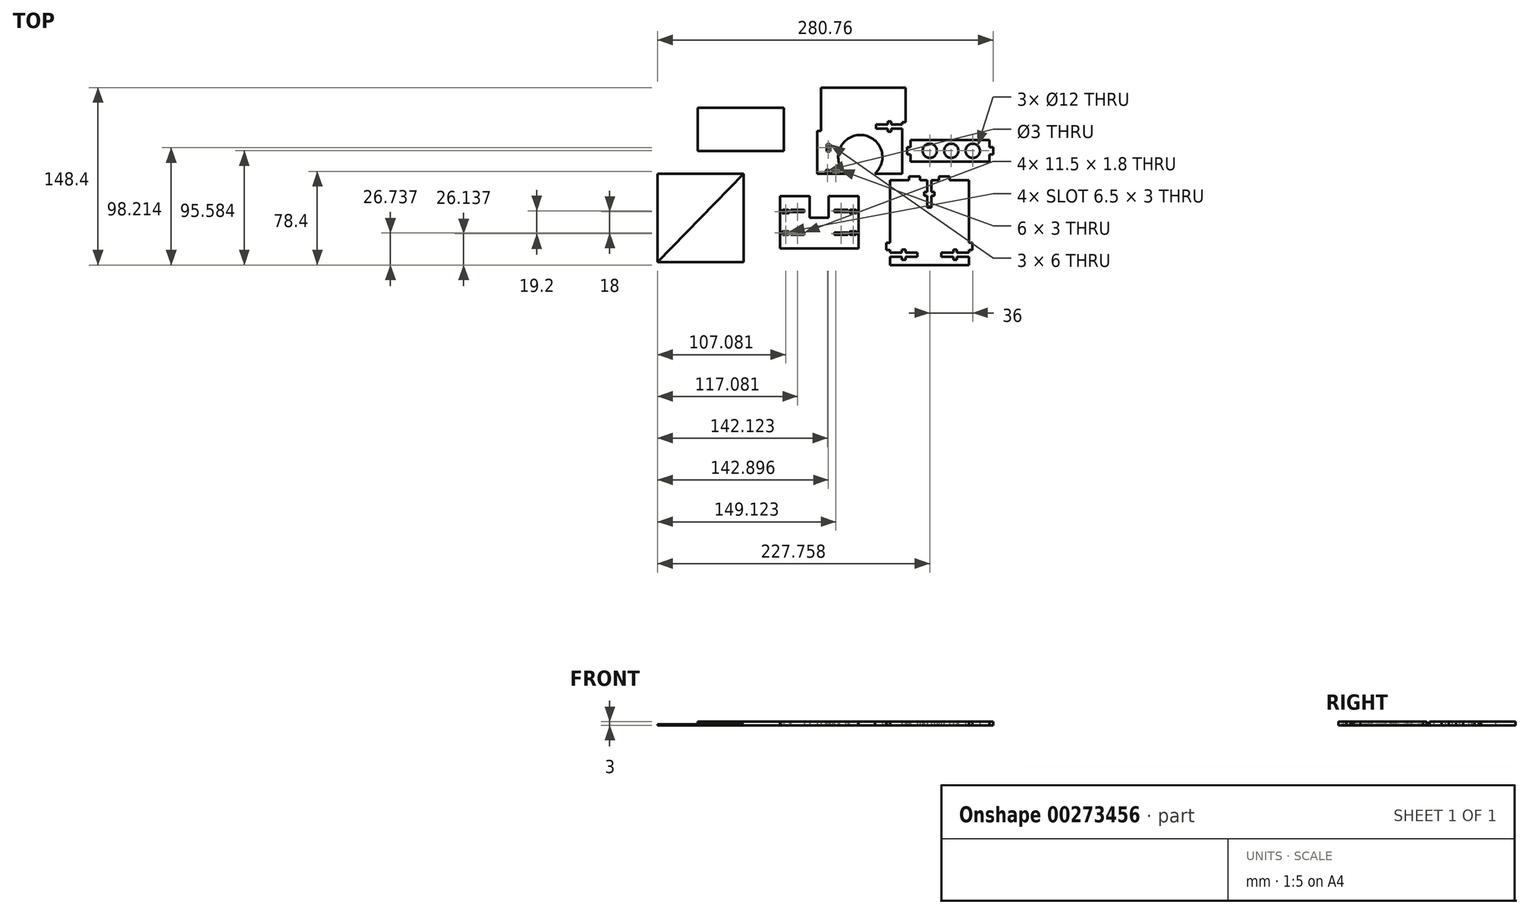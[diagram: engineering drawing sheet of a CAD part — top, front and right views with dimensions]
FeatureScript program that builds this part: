
annotation { "Feature Type Name" : "Feature", "Feature Type Description" : "" }
export const myFeature = defineFeature(function(context is Context, id is Id, definition is map)
    precondition{}
    {
        {
            var Q0;
            Q0=qCreatedBy(makeId("Top.planeOp"),FACE);
            var sketch = newSketch(context, id + "F0", { "sketchPlane" : qUnion([Q0])});
            skLineSegment(sketch, "E0", {"start": v(0, 0) * mm, "end": v(31.91, 0) * mm});
            skLineSegment(sketch, "E1", {"start": v(31.91, 0) * mm, "end": v(31.91, 36) * mm});
            skLineSegment(sketch, "E2", {"start": v(31.91, 36) * mm, "end": v(34.91, 36) * mm});
            skLineSegment(sketch, "E3", {"start": v(34.91, 36) * mm, "end": v(34.91, 72) * mm});
            skLineSegment(sketch, "E4", {"start": v(34.91, 72) * mm, "end": v(-36.09, 72) * mm});
            skLineSegment(sketch, "E5", {"start": v(-36.09, 72) * mm, "end": v(-36.09, 36) * mm});
            skLineSegment(sketch, "E6", {"start": v(-36.09, 36) * mm, "end": v(-39.09, 36) * mm});
            skLineSegment(sketch, "E7", {"start": v(-39.09, 36) * mm, "end": v(-39.09, 0) * mm});
            skLineSegment(sketch, "E8", {"start": v(-39.09, 0) * mm, "end": v(0, 0) * mm});
            skSolve(sketch);
        }
        {
            var Q0;
            Q0=makeQuery(id+"F0.imprint","IMPRINT",FACE,{"disambiguationData":[TD([[makeQuery(id+"F0.imprint","IMPRINT",EDGE,{"derivedFrom":sQuery(id+"F0.wireOp",EDGE,"E0")}),1.0]])]});
            extrude(context, id + "F1", {"entities" : qUnion([Q0]), "depth" : 3 * mm});
        }
        {
            var Q0;
            Q0=makeQuery(id+"F0.imprint","IMPRINT",FACE,{"disambiguationData":[TD([[makeQuery(id+"F0.imprint","IMPRINT",EDGE,{"derivedFrom":sQuery(id+"F0.wireOp",EDGE,"E0")}),1.0]])]});
            var sketch = newSketch(context, id + "F2", { "sketchPlane" : qUnion([Q0])});
            skCircle(sketch, "E9", {"center": v(-3.09, 14) * mm, "radius": 18.5 * mm});
            skCircle(sketch, "E10", {"center": v(-30.59, 2) * mm, "radius": 1.5 * mm});
            skLineSegment(sketch, "E11.bottom", {"start": v(-26.59, 3.5) * mm, "end": v(-20.59, 3.5) * mm});
            skLineSegment(sketch, "E11.top", {"start": v(-26.59, 0.5) * mm, "end": v(-20.59, 0.5) * mm});
            skLineSegment(sketch, "E11.left", {"start": v(-26.59, 3.5) * mm, "end": v(-26.59, 0.5) * mm});
            skLineSegment(sketch, "E11.right", {"start": v(-20.59, 3.5) * mm, "end": v(-20.59, 0.5) * mm});
            skLineSegment(sketch, "E12.bottom", {"start": v(-31.31, 24.81) * mm, "end": v(-28.31, 24.81) * mm});
            skLineSegment(sketch, "E12.top", {"start": v(-31.31, 18.81) * mm, "end": v(-28.31, 18.81) * mm});
            skLineSegment(sketch, "E12.left", {"start": v(-31.31, 24.81) * mm, "end": v(-31.31, 18.81) * mm});
            skLineSegment(sketch, "E12.right", {"start": v(-28.31, 24.81) * mm, "end": v(-28.31, 18.81) * mm});
            skSolve(sketch);
        }
        {
            var Q0;
            Q0 = qSketchRegion(id + "F2", true);
            extrude(context, id + "F3", {"entities" : qUnion([Q0]), "operationType" : NewBodyOperationType.REMOVE, "endBound" : BoundingType.UP_TO_NEXT, "depth" : 25 * mm});
        }
        {
            var Q0;
            Q0=makeQuery(id+"F1.opExtrude","CAP_FACE",FACE,{"disambiguationData":[OSD([sQuery(id+"F0.wireOp",EDGE,"E0"),sQuery(id+"F0.wireOp",EDGE,"E1"),sQuery(id+"F0.wireOp",EDGE,"E2"),sQuery(id+"F0.wireOp",EDGE,"E3"),sQuery(id+"F0.wireOp",EDGE,"E4"),sQuery(id+"F0.wireOp",EDGE,"E5"),sQuery(id+"F0.wireOp",EDGE,"E6"),sQuery(id+"F0.wireOp",EDGE,"E7"),sQuery(id+"F0.wireOp",EDGE,"E8")])],"isStart":false});
            var sketch = newSketch(context, id + "F4", { "sketchPlane" : qUnion([Q0])});
            skLineSegment(sketch, "E13", {"start": v(22.91, 41.25) * mm, "end": v(22.91, 43.75) * mm});
            skLineSegment(sketch, "E14", {"start": v(22.91, 43.75) * mm, "end": v(19.91, 43.75) * mm});
            skLineSegment(sketch, "E15", {"start": v(19.91, 43.75) * mm, "end": v(19.91, 41.25) * mm});
            skLineSegment(sketch, "E16", {"start": v(19.91, 41.25) * mm, "end": v(9.91, 41.25) * mm});
            skLineSegment(sketch, "E17", {"start": v(9.91, 41.25) * mm, "end": v(9.91, 37.75) * mm});
            skLineSegment(sketch, "E18", {"start": v(9.91, 37.75) * mm, "end": v(19.91, 37.75) * mm});
            skLineSegment(sketch, "E19", {"start": v(19.91, 37.75) * mm, "end": v(19.91, 35.25) * mm});
            skLineSegment(sketch, "E20", {"start": v(19.91, 35.25) * mm, "end": v(22.91, 35.25) * mm});
            skLineSegment(sketch, "E21", {"start": v(22.91, 35.25) * mm, "end": v(22.91, 37.75) * mm});
            skLineSegment(sketch, "E22", {"start": v(22.91, 41.25) * mm, "end": v(31.91, 41.25) * mm});
            skLineSegment(sketch, "E23", {"start": v(31.91, 36) * mm, "end": v(31.91, 37.75) * mm});
            skLineSegment(sketch, "E24", {"start": v(31.91, 37.75) * mm, "end": v(22.91, 37.75) * mm});
            skLineSegment(sketch, "E25", {"start": v(31.91, 41.25) * mm, "end": v(31.91, 43) * mm});
            skLineSegment(sketch, "E26", {"start": v(31.91, 43) * mm, "end": v(34.91, 43) * mm});
            skLineSegment(sketch, "E27", {"start": v(31.91, 36) * mm, "end": v(34.91, 36) * mm});
            skLineSegment(sketch, "E28", {"start": v(34.91, 36) * mm, "end": v(34.91, 43) * mm});
            skSolve(sketch);
        }
        {
            var Q0;
            Q0=makeQuery(id+"F4.imprint","IMPRINT",FACE,{"disambiguationData":[TD([[makeQuery(id+"F4.imprint","IMPRINT",EDGE,{"derivedFrom":sQuery(id+"F4.wireOp",EDGE,"E13")}),1.0]])]});
            var Q1;
            Q1=makeQuery(id+"F4.imprint","IMPRINT",FACE,{"disambiguationData":[TD([[makeQuery(id+"F4.imprint","IMPRINT",EDGE,{"derivedFrom":sQuery(id+"F4.wireOp",EDGE,"a1bc5330-3307-4b1e-8fa0-ecfa6d1ff466.1.0.0")}),1.0]])]});
            extrude(context, id + "F5", {"entities" : qUnion([Q0, Q1]), "operationType" : NewBodyOperationType.REMOVE, "endBound" : BoundingType.UP_TO_NEXT, "oppositeDirection" : true, "depth" : 25 * mm});
        }
        {
            var Q0;
            Q0=qCreatedBy(makeId("Top.planeOp"),FACE);
            var sketch = newSketch(context, id + "F6", { "sketchPlane" : qUnion([Q0])});
            skLineSegment(sketch, "E29.bottom", {"start": v(-70.38, -18.66) * mm, "end": v(-4.38, -18.66) * mm});
            skLineSegment(sketch, "E29.top", {"start": v(-70.38, -62.66) * mm, "end": v(-4.38, -62.66) * mm});
            skLineSegment(sketch, "E29.left", {"start": v(-70.38, -18.66) * mm, "end": v(-70.38, -62.66) * mm});
            skLineSegment(sketch, "E29.right", {"start": v(-4.38, -18.66) * mm, "end": v(-4.38, -62.66) * mm});
            skLineSegment(sketch, "E30.bottom", {"start": v(-61.38, -30.16) * mm, "end": v(-49.88, -30.16) * mm});
            skLineSegment(sketch, "E30.top", {"start": v(-61.38, -31.96) * mm, "end": v(-49.88, -31.96) * mm});
            skLineSegment(sketch, "E30.left", {"start": v(-61.38, -30.16) * mm, "end": v(-61.38, -31.96) * mm});
            skLineSegment(sketch, "E30.right", {"start": v(-49.88, -30.16) * mm, "end": v(-49.88, -31.96) * mm});
            skLineSegment(sketch, "E31.bottom", {"start": v(-67.38, -30.16) * mm, "end": v(-63.88, -30.16) * mm});
            skLineSegment(sketch, "E31.top", {"start": v(-67.38, -33.16) * mm, "end": v(-63.88, -33.16) * mm});
            skLineSegment(sketch, "E31.left", {"start": v(-68.88, -31.66) * mm, "end": v(-68.88, -31.66) * mm});
            skLineSegment(sketch, "E31.right", {"start": v(-62.38, -31.66) * mm, "end": v(-62.38, -31.66) * mm});
            skPoint(sketch, "E32.visualSharp", {"position": v(-68.88, -30.16) * mm});
            skArc(sketch, "E32.filletArc", {"start": v(-67.38, -30.16) * mm, "mid": v(-68.44, -30.6) * mm, "end": v(-68.88, -31.66) * mm});
            skPoint(sketch, "E33.visualSharp", {"position": v(-68.88, -33.16) * mm});
            skArc(sketch, "E33.filletArc", {"start": v(-68.88, -31.66) * mm, "mid": v(-68.44, -32.72) * mm, "end": v(-67.38, -33.16) * mm});
            skPoint(sketch, "E34.visualSharp", {"position": v(-62.38, -33.16) * mm});
            skArc(sketch, "E34.filletArc", {"start": v(-63.88, -33.16) * mm, "mid": v(-62.82, -32.72) * mm, "end": v(-62.38, -31.66) * mm});
            skPoint(sketch, "E35.visualSharp", {"position": v(-62.38, -30.16) * mm});
            skArc(sketch, "E35.filletArc", {"start": v(-62.38, -31.66) * mm, "mid": v(-62.82, -30.6) * mm, "end": v(-63.88, -30.16) * mm});
            skLineSegment(sketch, "E36", {"start": v(-70.38, -40.66) * mm, "end": v(-4.38, -40.66) * mm, "construction": true});
            skLineSegment(sketch, "E37", {"start": v(-37.38, -18.66) * mm, "end": v(-37.38, -62.66) * mm, "construction": true});
            skArc(sketch, "E38.MirrorCS", {"start": v(-12.38, -31.66) * mm, "mid": v(-11.94, -30.6) * mm, "end": v(-10.88, -30.16) * mm});
            skLineSegment(sketch, "E39.MirrorCS", {"start": v(-24.88, -30.16) * mm, "end": v(-24.88, -31.96) * mm});
            skLineSegment(sketch, "E40.MirrorCS", {"start": v(-13.38, -30.16) * mm, "end": v(-13.38, -31.96) * mm});
            skArc(sketch, "E41.MirrorCS", {"start": v(-10.88, -33.16) * mm, "mid": v(-11.94, -32.72) * mm, "end": v(-12.38, -31.66) * mm});
            skArc(sketch, "E42.MirrorCS", {"start": v(-5.88, -31.66) * mm, "mid": v(-6.32, -32.72) * mm, "end": v(-7.38, -33.16) * mm});
            skArc(sketch, "E43.MirrorCS", {"start": v(-7.38, -30.16) * mm, "mid": v(-6.32, -30.6) * mm, "end": v(-5.88, -31.66) * mm});
            skLineSegment(sketch, "E44.MirrorCS", {"start": v(-7.38, -30.16) * mm, "end": v(-10.88, -30.16) * mm});
            skLineSegment(sketch, "E45.MirrorCS", {"start": v(-7.38, -33.16) * mm, "end": v(-10.88, -33.16) * mm});
            skLineSegment(sketch, "E46.MirrorCS", {"start": v(-13.38, -30.16) * mm, "end": v(-24.88, -30.16) * mm});
            skLineSegment(sketch, "E47.MirrorCS", {"start": v(-13.38, -31.96) * mm, "end": v(-24.88, -31.96) * mm});
            skPoint(sketch, "E48.MirrorP", {"position": v(-12.38, -33.16) * mm});
            skPoint(sketch, "E49.MirrorP", {"position": v(-12.38, -30.16) * mm});
            skPoint(sketch, "E50.MirrorP", {"position": v(-5.88, -30.16) * mm});
            skPoint(sketch, "E51.MirrorP", {"position": v(-5.88, -33.16) * mm});
            skLineSegment(sketch, "E52.MirrorCS", {"start": v(-7.38, -51.16) * mm, "end": v(-10.88, -51.16) * mm});
            skLineSegment(sketch, "E53.MirrorCS", {"start": v(-7.38, -48.16) * mm, "end": v(-10.88, -48.16) * mm});
            skLineSegment(sketch, "E54.MirrorCS", {"start": v(-13.38, -51.16) * mm, "end": v(-24.88, -51.16) * mm});
            skLineSegment(sketch, "E55.MirrorCS", {"start": v(-13.38, -49.36) * mm, "end": v(-24.88, -49.36) * mm});
            skArc(sketch, "E56.MirrorCS", {"start": v(-62.38, -49.66) * mm, "mid": v(-62.82, -50.72) * mm, "end": v(-63.88, -51.16) * mm});
            skArc(sketch, "E57.MirrorCS", {"start": v(-63.88, -48.16) * mm, "mid": v(-62.82, -48.6) * mm, "end": v(-62.38, -49.66) * mm});
            skArc(sketch, "E58.MirrorCS", {"start": v(-68.88, -49.66) * mm, "mid": v(-68.44, -48.6) * mm, "end": v(-67.38, -48.16) * mm});
            skLineSegment(sketch, "E59.MirrorCS", {"start": v(-61.38, -51.16) * mm, "end": v(-61.38, -49.36) * mm});
            skLineSegment(sketch, "E60.MirrorCS", {"start": v(-49.88, -51.16) * mm, "end": v(-49.88, -49.36) * mm});
            skArc(sketch, "E61.MirrorCS", {"start": v(-67.38, -51.16) * mm, "mid": v(-68.44, -50.72) * mm, "end": v(-68.88, -49.66) * mm});
            skPoint(sketch, "E62.MirrorP", {"position": v(-62.38, -48.16) * mm});
            skPoint(sketch, "E63.MirrorP", {"position": v(-68.88, -48.16) * mm});
            skPoint(sketch, "E64.MirrorP", {"position": v(-62.38, -51.16) * mm});
            skLineSegment(sketch, "E65.MirrorCS", {"start": v(-67.38, -51.16) * mm, "end": v(-63.88, -51.16) * mm});
            skPoint(sketch, "E66.MirrorP", {"position": v(-68.88, -51.16) * mm});
            skLineSegment(sketch, "E67.MirrorCS", {"start": v(-67.38, -48.16) * mm, "end": v(-63.88, -48.16) * mm});
            skLineSegment(sketch, "E68.MirrorCS", {"start": v(-61.38, -49.36) * mm, "end": v(-49.88, -49.36) * mm});
            skLineSegment(sketch, "E69.MirrorCS", {"start": v(-61.38, -51.16) * mm, "end": v(-49.88, -51.16) * mm});
            skArc(sketch, "E70.MirrorCS", {"start": v(-7.38, -51.16) * mm, "mid": v(-6.32, -50.72) * mm, "end": v(-5.88, -49.66) * mm});
            skLineSegment(sketch, "E71.MirrorCS", {"start": v(-13.38, -51.16) * mm, "end": v(-13.38, -49.36) * mm});
            skLineSegment(sketch, "E72.MirrorCS", {"start": v(-24.88, -51.16) * mm, "end": v(-24.88, -49.36) * mm});
            skArc(sketch, "E73.MirrorCS", {"start": v(-10.88, -48.16) * mm, "mid": v(-11.94, -48.6) * mm, "end": v(-12.38, -49.66) * mm});
            skArc(sketch, "E74.MirrorCS", {"start": v(-12.38, -49.66) * mm, "mid": v(-11.94, -50.72) * mm, "end": v(-10.88, -51.16) * mm});
            skArc(sketch, "E75.MirrorCS", {"start": v(-5.88, -49.66) * mm, "mid": v(-6.32, -48.6) * mm, "end": v(-7.38, -48.16) * mm});
            skLineSegment(sketch, "E76.bottom", {"start": v(-45.43, -18.66) * mm, "end": v(-29.7, -18.66) * mm});
            skLineSegment(sketch, "E76.top", {"start": v(-45.43, -36.8) * mm, "end": v(-29.7, -36.8) * mm});
            skLineSegment(sketch, "E76.left", {"start": v(-45.43, -18.66) * mm, "end": v(-45.43, -36.8) * mm});
            skLineSegment(sketch, "E76.right", {"start": v(-29.7, -18.66) * mm, "end": v(-29.7, -36.8) * mm});
            skSolve(sketch);
        }
        {
            var Q0;
            Q0=makeQuery(id+"F6.imprint","IMPRINT",FACE,{"disambiguationData":[TD([[makeQuery(id+"F6.imprint","IMPRINT",EDGE,{"derivedFrom":sQuery(id+"F6.wireOp",EDGE,"E29.bottom")}),-1.0]])]});
            extrude(context, id + "F7", {"entities" : qUnion([Q0]), "depth" : 3 * mm});
        }
        {
            var Q0;
            Q0=qCreatedBy(makeId("Top.planeOp"),FACE);
            var sketch = newSketch(context, id + "F8", { "sketchPlane" : qUnion([Q0])});
            skLineSegment(sketch, "E77.bottom", {"start": v(-67.1, 19.07) * mm, "end": v(-139.1, 19.07) * mm});
            skLineSegment(sketch, "E77.top", {"start": v(-67.1, 55.07) * mm, "end": v(-139.1, 55.07) * mm});
            skLineSegment(sketch, "E77.left", {"start": v(-67.1, 19.07) * mm, "end": v(-67.1, 55.07) * mm});
            skLineSegment(sketch, "E77.right", {"start": v(-139.1, 19.07) * mm, "end": v(-139.1, 55.07) * mm});
            skSolve(sketch);
        }
        {
            var Q0;
            Q0=makeQuery(id+"F8.imprint","IMPRINT",FACE,{"disambiguationData":[TD([[makeQuery(id+"F8.imprint","IMPRINT",EDGE,{"derivedFrom":sQuery(id+"F8.wireOp",EDGE,"E77.bottom")}),-1.0]])]});
            extrude(context, id + "F9", {"entities" : qUnion([Q0]), "depth" : 3 * mm});
        }
        {
            var Q0;
            Q0=qCreatedBy(makeId("Top.planeOp"),FACE);
            var sketch = newSketch(context, id + "F10", { "sketchPlane" : qUnion([Q0])});
            skLineSegment(sketch, "E78.bottom", {"start": v(21.76, -5.4) * mm, "end": v(37.76, -5.4) * mm});
            skLineSegment(sketch, "E78.top", {"start": v(21.76, -76.4) * mm, "end": v(87.76, -76.4) * mm});
            skLineSegment(sketch, "E78.left", {"start": v(21.76, -5.4) * mm, "end": v(21.76, -57.9) * mm});
            skLineSegment(sketch, "E78.right", {"start": v(87.76, -5.4) * mm, "end": v(87.76, -57.9) * mm});
            skLineSegment(sketch, "E79", {"start": v(53.01, -5.4) * mm, "end": v(53.01, -15.4) * mm});
            skLineSegment(sketch, "E80", {"start": v(53.01, -15.4) * mm, "end": v(50.51, -15.4) * mm});
            skLineSegment(sketch, "E81", {"start": v(50.51, -15.4) * mm, "end": v(50.51, -18.4) * mm});
            skLineSegment(sketch, "E82", {"start": v(50.51, -18.4) * mm, "end": v(53.01, -18.4) * mm});
            skLineSegment(sketch, "E83", {"start": v(53.01, -18.4) * mm, "end": v(53.01, -28.4) * mm});
            skLineSegment(sketch, "E84", {"start": v(53.01, -28.4) * mm, "end": v(56.51, -28.4) * mm});
            skLineSegment(sketch, "E85", {"start": v(56.51, -28.4) * mm, "end": v(56.51, -18.4) * mm});
            skLineSegment(sketch, "E86", {"start": v(56.51, -18.4) * mm, "end": v(59.01, -18.4) * mm});
            skLineSegment(sketch, "E87", {"start": v(59.01, -18.4) * mm, "end": v(59.01, -15.4) * mm});
            skLineSegment(sketch, "E88", {"start": v(59.01, -15.4) * mm, "end": v(56.51, -15.4) * mm});
            skLineSegment(sketch, "E89", {"start": v(56.51, -15.4) * mm, "end": v(56.51, -5.4) * mm});
            skLineSegment(sketch, "E90", {"start": v(50.51, -15.4) * mm, "end": v(21.76, -15.4) * mm, "construction": true});
            skLineSegment(sketch, "E91", {"start": v(59.01, -15.4) * mm, "end": v(87.76, -15.4) * mm, "construction": true});
            skLineSegment(sketch, "E92", {"start": v(21.76, -69.65) * mm, "end": v(31.76, -69.65) * mm});
            skLineSegment(sketch, "E93", {"start": v(31.76, -69.65) * mm, "end": v(31.76, -72.15) * mm});
            skLineSegment(sketch, "E94", {"start": v(31.76, -72.15) * mm, "end": v(34.76, -72.15) * mm});
            skLineSegment(sketch, "E95", {"start": v(34.76, -72.15) * mm, "end": v(34.76, -69.65) * mm});
            skLineSegment(sketch, "E96", {"start": v(34.76, -69.65) * mm, "end": v(44.76, -69.65) * mm});
            skLineSegment(sketch, "E97", {"start": v(44.76, -69.65) * mm, "end": v(44.76, -66.15) * mm});
            skLineSegment(sketch, "E98", {"start": v(44.76, -66.15) * mm, "end": v(34.76, -66.15) * mm});
            skLineSegment(sketch, "E99", {"start": v(34.76, -66.15) * mm, "end": v(34.76, -63.65) * mm});
            skLineSegment(sketch, "E100", {"start": v(34.76, -63.65) * mm, "end": v(31.76, -63.65) * mm});
            skLineSegment(sketch, "E101", {"start": v(31.76, -63.65) * mm, "end": v(31.76, -66.15) * mm});
            skLineSegment(sketch, "E102", {"start": v(31.76, -66.15) * mm, "end": v(21.76, -66.15) * mm});
            skLineSegment(sketch, "E103", {"start": v(54.76, -76.4) * mm, "end": v(54.76, -55.52) * mm, "construction": true});
            skLineSegment(sketch, "E104.MirrorCS", {"start": v(74.76, -63.65) * mm, "end": v(77.76, -63.65) * mm});
            skLineSegment(sketch, "E105.MirrorCS", {"start": v(77.76, -69.65) * mm, "end": v(77.76, -72.15) * mm});
            skLineSegment(sketch, "E106.MirrorCS", {"start": v(77.76, -66.15) * mm, "end": v(87.76, -66.15) * mm});
            skLineSegment(sketch, "E107.MirrorCS", {"start": v(74.76, -72.15) * mm, "end": v(74.76, -69.65) * mm});
            skLineSegment(sketch, "E108.MirrorCS", {"start": v(77.76, -72.15) * mm, "end": v(74.76, -72.15) * mm});
            skLineSegment(sketch, "E109.MirrorCS", {"start": v(74.76, -69.65) * mm, "end": v(64.76, -69.65) * mm});
            skLineSegment(sketch, "E110.MirrorCS", {"start": v(64.76, -66.15) * mm, "end": v(74.76, -66.15) * mm});
            skLineSegment(sketch, "E111.MirrorCS", {"start": v(74.76, -66.15) * mm, "end": v(74.76, -63.65) * mm});
            skLineSegment(sketch, "E112.MirrorCS", {"start": v(87.76, -69.65) * mm, "end": v(77.76, -69.65) * mm});
            skLineSegment(sketch, "E113.MirrorCS", {"start": v(64.76, -69.65) * mm, "end": v(64.76, -66.15) * mm});
            skLineSegment(sketch, "E114.MirrorCS", {"start": v(77.76, -63.65) * mm, "end": v(77.76, -66.15) * mm});
            skLineSegment(sketch, "E115.bottom", {"start": v(87.76, -63.9) * mm, "end": v(90.76, -63.9) * mm});
            skLineSegment(sketch, "E115.top", {"start": v(87.76, -57.9) * mm, "end": v(90.76, -57.9) * mm});
            skLineSegment(sketch, "E115.right", {"start": v(90.76, -63.9) * mm, "end": v(90.76, -57.9) * mm});
            skLineSegment(sketch, "E116.trimOffspring", {"start": v(87.76, -63.9) * mm, "end": v(87.76, -76.4) * mm});
            skLineSegment(sketch, "E117.MirrorCS", {"start": v(21.76, -63.9) * mm, "end": v(18.76, -63.9) * mm});
            skLineSegment(sketch, "E118.MirrorCS", {"start": v(21.76, -57.9) * mm, "end": v(18.76, -57.9) * mm});
            skLineSegment(sketch, "E119.MirrorCS", {"start": v(18.76, -63.9) * mm, "end": v(18.76, -57.9) * mm});
            skLineSegment(sketch, "E120.trimOffspring", {"start": v(21.76, -63.9) * mm, "end": v(21.76, -76.4) * mm});
            skLineSegment(sketch, "E121.top", {"start": v(62.76, -2.4) * mm, "end": v(71.76, -2.4) * mm});
            skLineSegment(sketch, "E121.left", {"start": v(62.76, -5.4) * mm, "end": v(62.76, -2.4) * mm});
            skLineSegment(sketch, "E121.right", {"start": v(71.76, -5.4) * mm, "end": v(71.76, -2.4) * mm});
            skLineSegment(sketch, "E122", {"start": v(54.76, -5.4) * mm, "end": v(54.76, -1.03) * mm, "construction": true});
            skLineSegment(sketch, "E123.trimOffspring", {"start": v(71.76, -5.4) * mm, "end": v(87.76, -5.4) * mm});
            skLineSegment(sketch, "E124.MirrorCS", {"start": v(46.76, -5.4) * mm, "end": v(46.76, -2.4) * mm});
            skLineSegment(sketch, "E125.MirrorCS", {"start": v(37.76, -5.4) * mm, "end": v(37.76, -2.4) * mm});
            skLineSegment(sketch, "E126.MirrorCS", {"start": v(46.76, -2.4) * mm, "end": v(37.76, -2.4) * mm});
            skLineSegment(sketch, "E127.trimOffspring", {"start": v(46.76, -5.4) * mm, "end": v(62.76, -5.4) * mm});
            skSolve(sketch);
        }
        {
            var Q0;
            Q0=makeQuery(id+"F10.imprint","IMPRINT",FACE,{"disambiguationData":[TD([[makeQuery(id+"F10.imprint","IMPRINT",EDGE,{"derivedFrom":sQuery(id+"F10.wireOp",EDGE,"E78.bottom")}),-1.0]])]});
            extrude(context, id + "F11", {"entities" : qUnion([Q0]), "depth" : 3 * mm});
        }
        {
            var Q0;
            Q0=qCreatedBy(makeId("Top.planeOp"),FACE);
            var sketch = newSketch(context, id + "F12", { "sketchPlane" : qUnion([Q0])});
            skLineSegment(sketch, "E128.bottom", {"start": v(-172.7, -0.16) * mm, "end": v(-100.7, -0.16) * mm});
            skLineSegment(sketch, "E128.top", {"start": v(-172.7, -74.16) * mm, "end": v(-100.7, -74.16) * mm});
            skLineSegment(sketch, "E128.left", {"start": v(-172.7, -0.16) * mm, "end": v(-172.7, -74.16) * mm});
            skLineSegment(sketch, "E128.right", {"start": v(-100.7, -0.16) * mm, "end": v(-100.7, -74.16) * mm});
            skLineSegment(sketch, "E129", {"start": v(-172.7, -74.16) * mm, "end": v(-100.7, -0.16) * mm});
            skSolve(sketch);
        }
        {
            var Q0;
            Q0=makeQuery(id+"F12.imprint","IMPRINT",FACE,{"disambiguationData":[TD([[makeQuery(id+"F12.imprint","IMPRINT",EDGE,{"derivedFrom":sQuery(id+"F12.wireOp",EDGE,"E128.bottom")}),-1.0]])]});
            extrude(context, id + "F13", {"entities" : qUnion([Q0]), "depth" : 1 * mm});
        }
        {
            var Q0;
            Q0=makeQuery(id+"F12.imprint","IMPRINT",FACE,{"disambiguationData":[TD([[makeQuery(id+"F12.imprint","IMPRINT",EDGE,{"derivedFrom":sQuery(id+"F12.wireOp",EDGE,"E128.top")}),1.0]])]});
            extrude(context, id + "F14", {"entities" : qUnion([Q0]), "depth" : 1 * mm});
        }
        {
            var Q0;
            Q0=qCreatedBy(makeId("Top.planeOp"),FACE);
            var sketch = newSketch(context, id + "F15", { "sketchPlane" : qUnion([Q0])});
            skLineSegment(sketch, "E130", {"start": v(36.05, 16.18) * mm, "end": v(36.05, 22.18) * mm});
            skLineSegment(sketch, "E131", {"start": v(36.05, 22.18) * mm, "end": v(39.05, 22.18) * mm});
            skLineSegment(sketch, "E132", {"start": v(39.05, 22.18) * mm, "end": v(39.05, 28.18) * mm});
            skLineSegment(sketch, "E133", {"start": v(39.05, 28.18) * mm, "end": v(105.05, 28.18) * mm});
            skLineSegment(sketch, "E134", {"start": v(105.05, 28.18) * mm, "end": v(105.05, 22.18) * mm});
            skLineSegment(sketch, "E135", {"start": v(105.05, 22.18) * mm, "end": v(108.05, 22.18) * mm});
            skLineSegment(sketch, "E136", {"start": v(108.05, 22.18) * mm, "end": v(108.05, 16.18) * mm});
            skLineSegment(sketch, "E137", {"start": v(108.05, 16.18) * mm, "end": v(105.05, 16.18) * mm});
            skLineSegment(sketch, "E138", {"start": v(105.05, 16.18) * mm, "end": v(105.05, 10.18) * mm});
            skLineSegment(sketch, "E139", {"start": v(105.05, 10.18) * mm, "end": v(39.05, 10.18) * mm});
            skLineSegment(sketch, "E140", {"start": v(39.05, 10.18) * mm, "end": v(39.05, 16.18) * mm});
            skLineSegment(sketch, "E141", {"start": v(39.05, 16.18) * mm, "end": v(36.05, 16.18) * mm});
            skCircle(sketch, "E142", {"center": v(55.05, 19.18) * mm, "radius": 6 * mm});
            skCircle(sketch, "E143.1.0.0", {"center": v(73.05, 19.18) * mm, "radius": 6 * mm});
            skCircle(sketch, "E143.2.0.0", {"center": v(91.05, 19.18) * mm, "radius": 6 * mm});
            skLineSegment(sketch, "E143.direction1", {"start": v(55.05, 19.18) * mm, "end": v(73.05, 19.18) * mm, "construction": true});
            skSolve(sketch);
        }
        {
            var Q0;
            Q0=makeQuery(id+"F15.imprint","IMPRINT",FACE,{"disambiguationData":[TD([[makeQuery(id+"F15.imprint","IMPRINT",EDGE,{"derivedFrom":sQuery(id+"F15.wireOp",EDGE,"E130")}),-1.0]])]});
            extrude(context, id + "F16", {"entities" : qUnion([Q0]), "depth" : 3 * mm});
        }
    });
